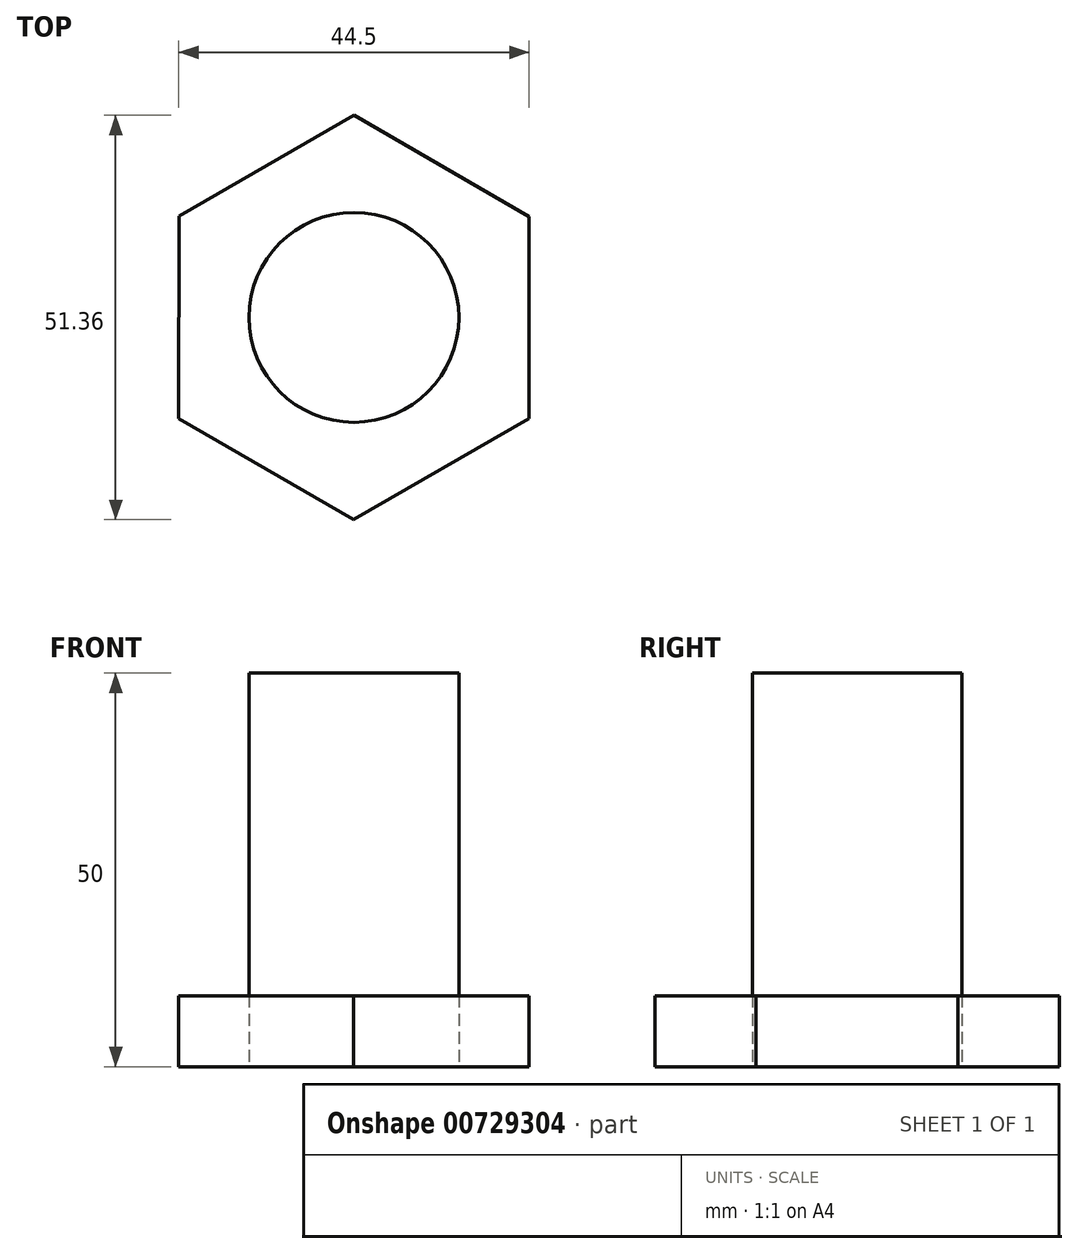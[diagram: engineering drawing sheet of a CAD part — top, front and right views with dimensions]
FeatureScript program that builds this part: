
annotation { "Feature Type Name" : "Feature", "Feature Type Description" : "" }
export const myFeature = defineFeature(function(context is Context, id is Id, definition is map)
    precondition{}
    {
        {
            var Q0;
            Q0=qCreatedBy(makeId("Top.planeOp"),FACE);
            var sketch = newSketch(context, id + "F0", { "sketchPlane" : qUnion([Q0])});
            skCircle(sketch, "E0.cCircle", {"center": v(0, 0) * mm, "radius": 22.24 * mm, "construction": true});
            skLineSegment(sketch, "E0.0", {"start": v(0.02, 25.68) * mm, "end": v(22.25, 12.82) * mm});
            skLineSegment(sketch, "E0.1", {"start": v(22.25, 12.82) * mm, "end": v(22.23, -12.86) * mm});
            skLineSegment(sketch, "E0.2", {"start": v(22.23, -12.86) * mm, "end": v(-0.02, -25.68) * mm});
            skLineSegment(sketch, "E0.3", {"start": v(-0.02, -25.68) * mm, "end": v(-22.25, -12.82) * mm});
            skLineSegment(sketch, "E0.4", {"start": v(-22.25, -12.82) * mm, "end": v(-22.23, 12.86) * mm});
            skLineSegment(sketch, "E0.5", {"start": v(-22.23, 12.86) * mm, "end": v(0.02, 25.68) * mm});
            skPoint(sketch, "E0.0.midPoint", {"position": v(11.14, 19.25) * mm});
            skSolve(sketch);
        }
        {
            var Q0;
            Q0 = qSketchRegion(id + "F0", true);
            extrude(context, id + "F1", {"entities" : qUnion([Q0]), "depth" : 9 * mm, "offsetDistance" : 25.4 * mm});
        }
        {
            var Q0;
            Q0=qCreatedBy(makeId("Top.planeOp"),FACE);
            var sketch = newSketch(context, id + "F2", { "sketchPlane" : qUnion([Q0])});
            skCircle(sketch, "E1", {"center": v(0, 0) * mm, "radius": 13.33 * mm});
            skSolve(sketch);
        }
        {
            var Q0;
            Q0 = qSketchRegion(id + "F2", true);
            var Q1;
            Q1 = qBodyType(qCreatedBy(id + "F2" ,EDGE), BodyType.WIRE);
            extrude(context, id + "F3", {"entities" : qUnion([Q0]), "surfaceEntities" : qUnion([Q1]), "depth" : 50 * mm, "offsetDistance" : 25.4 * mm});
        }
    });
